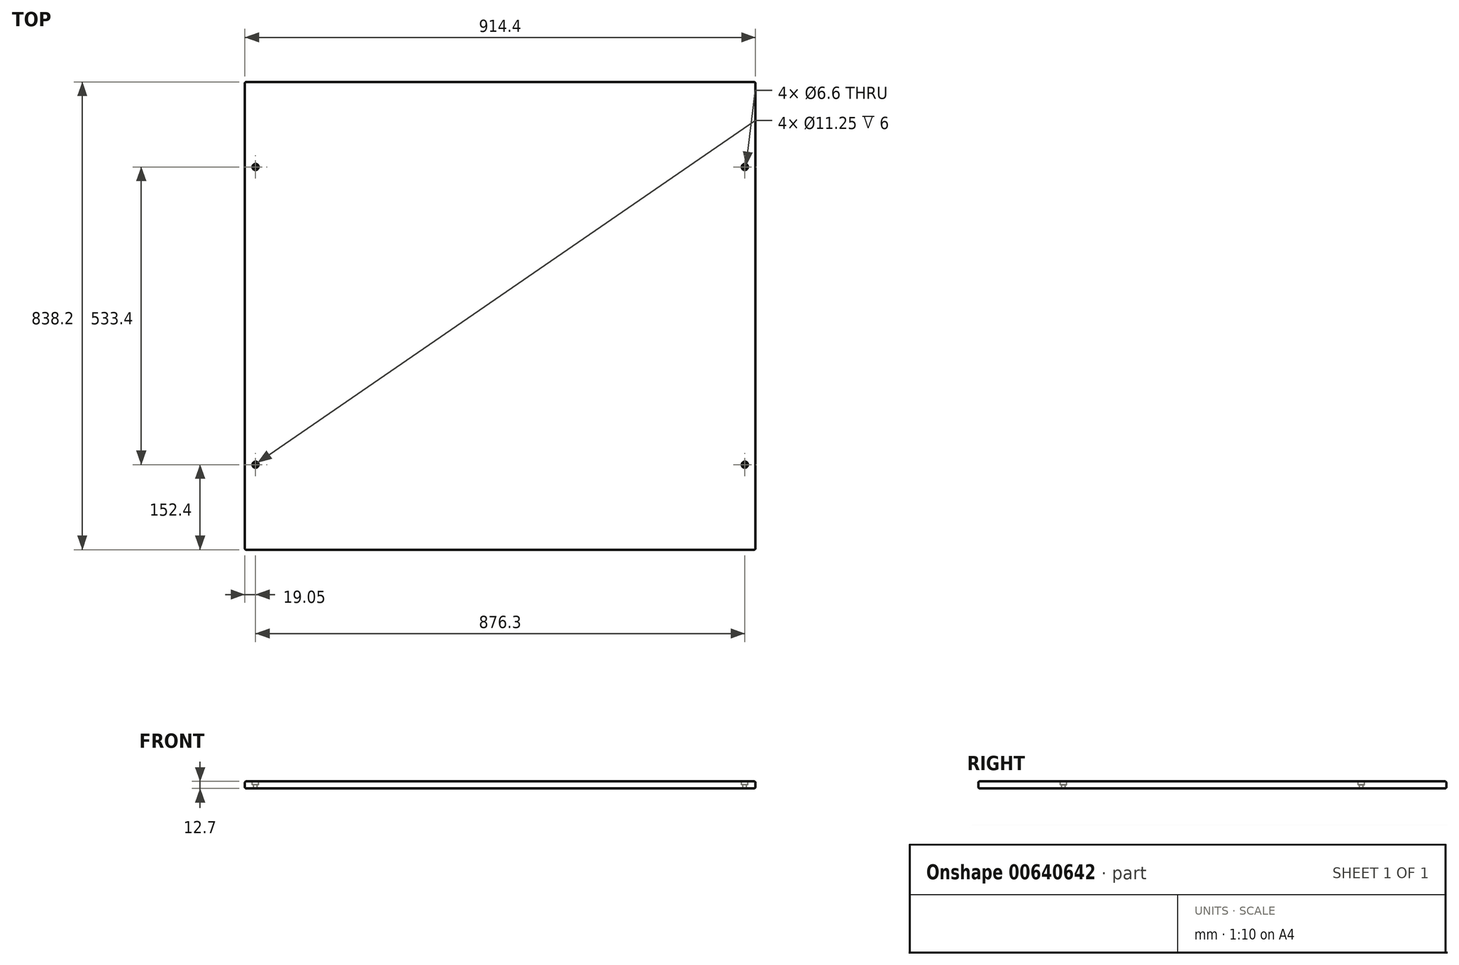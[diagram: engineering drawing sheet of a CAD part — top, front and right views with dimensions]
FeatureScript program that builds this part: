
annotation { "Feature Type Name" : "Feature", "Feature Type Description" : "" }
export const myFeature = defineFeature(function(context is Context, id is Id, definition is map)
    precondition{}
    {
        {
            var Q0;
            Q0=qCreatedBy(makeId("Top.planeOp"),FACE);
            var sketch = newSketch(context, id + "F0", { "sketchPlane" : qUnion([Q0])});
            skLineSegment(sketch, "E0.bottom", {"start": v(457.2, -419.1) * mm, "end": v(-457.2, -419.1) * mm});
            skLineSegment(sketch, "E0.top", {"start": v(457.2, 419.1) * mm, "end": v(-457.2, 419.1) * mm});
            skLineSegment(sketch, "E0.left", {"start": v(457.2, -419.1) * mm, "end": v(457.2, 419.1) * mm});
            skLineSegment(sketch, "E0.right", {"start": v(-457.2, -419.1) * mm, "end": v(-457.2, 419.1) * mm});
            skPoint(sketch, "E0.middle", {"position": v(0, 0) * mm});
            skSolve(sketch);
        }
        {
            var Q0;
            Q0=makeQuery(id+"F0.imprint","IMPRINT",FACE,{"disambiguationData":[TD([[makeQuery(id+"F0.imprint","IMPRINT",EDGE,{"derivedFrom":sQuery(id+"F0.wireOp",EDGE,"E0.bottom")}),-1.0]])]});
            extrude(context, id + "F1", {"entities" : qUnion([Q0]), "depth" : 12.7 * mm, "offsetDistance" : 25.4 * mm});
        }
        {
            var Q0;
            Q0=makeQuery(id+"F1.opExtrude","CAP_FACE",FACE,{"disambiguationData":[OSD([sQuery(id+"F0.wireOp",EDGE,"E0.bottom"),sQuery(id+"F0.wireOp",EDGE,"E0.top"),sQuery(id+"F0.wireOp",EDGE,"E0.left"),sQuery(id+"F0.wireOp",EDGE,"E0.right")])],"isStart":false});
            var sketch = newSketch(context, id + "F2", { "sketchPlane" : qUnion([Q0])});
            skPoint(sketch, "E1", {"position": v(-438.15, 266.7) * mm});
            skPoint(sketch, "E2.MirrorP", {"position": v(438.15, 266.7) * mm});
            skPoint(sketch, "E3.MirrorP", {"position": v(-438.15, -266.7) * mm});
            skPoint(sketch, "E4.MirrorP", {"position": v(438.15, -266.7) * mm});
            skSolve(sketch);
        }
        {
            var Q0;
            Q0=makeQuery(id+"F1.opExtrude","SWEPT_FACE",FACE,{"disambiguationData":[OSD([sQuery(id+"F0.wireOp",EDGE,"E0.left")])]});
            var Q1;
            Q1=makeQuery(id+"F1.opExtrude","SWEPT_FACE",FACE,{"disambiguationData":[OSD([sQuery(id+"F0.wireOp",EDGE,"E0.top")])]});
            var Q2;
            Q2=makeQuery(id+"F1.opExtrude","SWEPT_FACE",FACE,{"disambiguationData":[OSD([sQuery(id+"F0.wireOp",EDGE,"E0.right")])]});
            var Q3;
            Q3=makeQuery(id+"F1.opExtrude","SWEPT_FACE",FACE,{"disambiguationData":[OSD([sQuery(id+"F0.wireOp",EDGE,"E0.bottom")])]});
            fillet(context, id + "F3", {"entities" : qUnion([Q0, Q1, Q2, Q3]), "radius" : 2.54 * mm, "tangentPropagation" : true, "allowEdgeOverflow" : false});
        }
        {
            var Q0;
            Q0=sQuery(id+"F2.wireOp",VERTEX,"E3.MirrorP");
            var Q1;
            Q1=sQuery(id+"F2.wireOp",VERTEX,"E1");
            var Q2;
            Q2=sQuery(id+"F2.wireOp",VERTEX,"E2.MirrorP");
            var Q3;
            Q3=sQuery(id+"F2.wireOp",VERTEX,"E4.MirrorP");
            var Q4;
            Q4=makeQuery(id+"F1.opExtrude","SWEPT_BODY",BODY,{"disambiguationData":[OSD([sQuery(id+"F0.wireOp",EDGE,"E0.bottom"),sQuery(id+"F0.wireOp",EDGE,"E0.top"),sQuery(id+"F0.wireOp",EDGE,"E0.left"),sQuery(id+"F0.wireOp",EDGE,"E0.right")])]});
            hole(context, id + "F4", {"style" : HoleStyle.C_BORE, "endStyle" : HoleEndStyle.THROUGH, "standardTappedOrClearance" : lookupTablePath({ "standard" : "ISO", "fit" : "Normal", "size" : "M6", "type" : "Clearance" }), "standardBlindInLast" : lookupTablePath({ "fit" : "Standard", "standard" : "ISO", "size" : "M6", "type" : "Clearance" }), "holeDiameter" : 6.6 * mm, "cBoreDiameter" : 11.25 * mm, "cBoreDepth" : 6 * mm, "majorDiameter" : 3 * mm, "isTappedThrough" : true, "tappedDepth" : 3.62 * mm, "tapClearance" : 8, "startFromSketch" : true, "locations" : qUnion([Q0, Q1, Q2, Q3]), "scope" : qUnion([Q4])});
        }
    });
